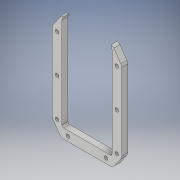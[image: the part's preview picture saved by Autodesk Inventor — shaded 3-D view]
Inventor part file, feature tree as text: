
AUTODESK INVENTOR PART (.ipt)
format: ipt  version: 2019 (Build 230136000, 136)  size: 164,864 bytes
history: native  units: in
note: dims shown in document units (in); Inventor stores cm internally (conversion verified against a paired STEP export)
features: sketch x1, extrude x1
ambient origin geometry x8: Origin, YZ Plane, XZ Plane, XY Plane, X Axis, Y Axis, Z Axis, Center Point
bodies: Solid1 (feature_tree)
feature tree (2):
  sketch  "Sketch1"  dims[d0=0.1378in d1=0.0in d2=0.0394in d3=0.0787in d4=0.0787in d5=0.0394in d6=0.0787in]
  extrude  "Extrusion1"  Depth=0.0394in
